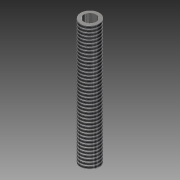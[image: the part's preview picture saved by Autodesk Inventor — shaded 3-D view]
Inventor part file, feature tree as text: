
AUTODESK INVENTOR PART (.ipt)
format: ipt  version: 2013 (Build 170138000, 138)  size: 90,112 bytes
history: native  units: mm
features: extrude x1, thread x1, sketch x1
ambient origin geometry x8: Origin, YZ Plane, XZ Plane, XY Plane, X Axis, Y Axis, Z Axis, Center Point
bodies: Solid1 (feature_tree)
feature tree (3):
  extrude  "Extrusion1"  Depth=6.0mm
  thread  "Thread1"  [1 undecoded]
  sketch  "Sketch1"  dims[d0=4.0mm d2=6.0mm d3=40.0mm d4=0.0mm d5=10.0mm d6=0.0mm]
note: 1 required parameter value undecoded (feature->parameter linkage not recoverable at this tier; creation-order binding heuristic only, values carry confidence <= 0.55)
